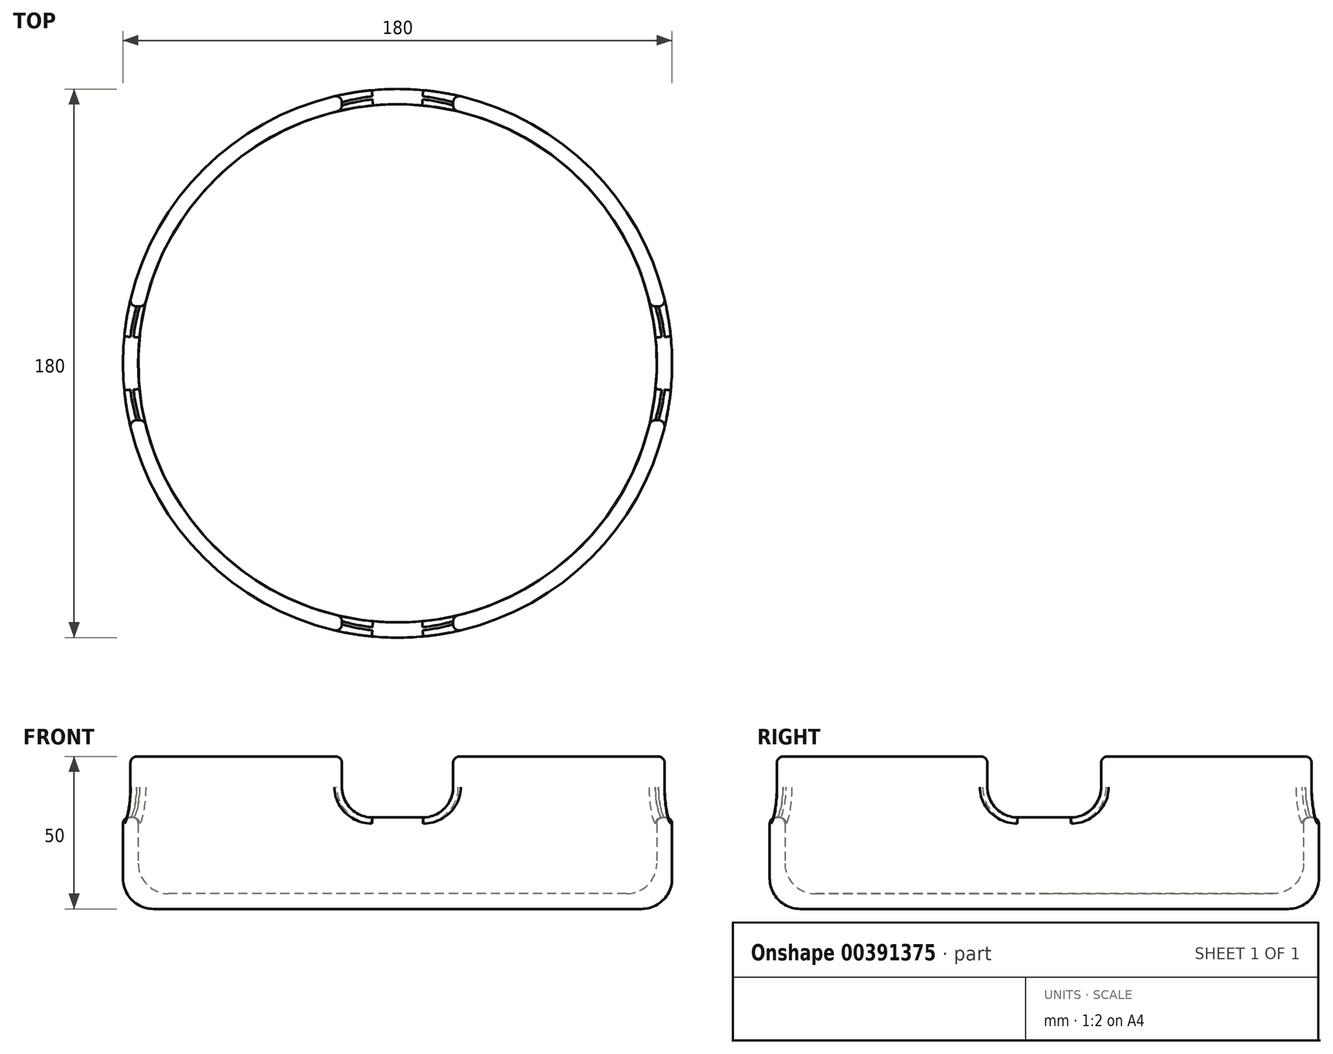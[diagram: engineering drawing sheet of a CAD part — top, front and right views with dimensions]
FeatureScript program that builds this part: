
annotation { "Feature Type Name" : "Feature", "Feature Type Description" : "" }
export const myFeature = defineFeature(function(context is Context, id is Id, definition is map)
    precondition{}
    {
        {
            var Q0;
            Q0=qCreatedBy(makeId("Top.planeOp"),FACE);
            var sketch = newSketch(context, id + "F0", { "sketchPlane" : qUnion([Q0])});
            skCircle(sketch, "E0", {"center": v(0, 0) * mm, "radius": 90 * mm});
            skSolve(sketch);
        }
        {
            var Q0;
            Q0=makeQuery(id+"F0.imprint","IMPRINT",FACE,{"disambiguationData":[TD([[makeQuery(id+"F0.imprint","IMPRINT",EDGE,{"derivedFrom":sQuery(id+"F0.wireOp",EDGE,"E0")}),1.0]])]});
            extrude(context, id + "F1", {"entities" : qUnion([Q0]), "depth" : 50 * mm});
        }
        {
            var Q0;
            Q0=makeQuery(id+"F1.opExtrude","CAP_FACE",FACE,{"disambiguationData":[OSD([sQuery(id+"F0.wireOp",EDGE,"E0")])],"isStart":false});
            shell(context, id + "F2", {"entities" : qUnion([Q0]), "thickness" : 5 * mm});
        }
        {
            var Q0;
            Q0=qCreatedBy(makeId("Top.planeOp"),FACE);
            cPlane(context, id + "F3", {"entities" : qUnion([Q0]), "cplaneType" : CPlaneType.OFFSET, "offset" : 50 * mm, "width" : 152.4 * mm, "height" : 152.4 * mm});
        }
        {
            var Q0;
            Q0=qCreatedBy(id+"F3.planeOp",FACE);
            var sketch = newSketch(context, id + "F4", { "sketchPlane" : qUnion([Q0])});
            skLineSegment(sketch, "E1.bottom", {"start": v(18.24, -119.27) * mm, "end": v(-18.24, -119.27) * mm});
            skLineSegment(sketch, "E1.top", {"start": v(18.24, 119.27) * mm, "end": v(-18.24, 119.27) * mm});
            skLineSegment(sketch, "E1.left", {"start": v(18.24, -119.27) * mm, "end": v(18.24, 119.27) * mm});
            skLineSegment(sketch, "E1.right", {"start": v(-18.24, -119.27) * mm, "end": v(-18.24, 119.27) * mm});
            skPoint(sketch, "E1.middle", {"position": v(0, 0) * mm});
            skLineSegment(sketch, "E2.bottom", {"start": v(-104.63, 18.65) * mm, "end": v(104.63, 18.65) * mm});
            skLineSegment(sketch, "E2.top", {"start": v(-104.63, -18.65) * mm, "end": v(104.63, -18.65) * mm});
            skLineSegment(sketch, "E2.left", {"start": v(-104.63, 18.65) * mm, "end": v(-104.63, -18.65) * mm});
            skLineSegment(sketch, "E2.right", {"start": v(104.63, 18.65) * mm, "end": v(104.63, -18.65) * mm});
            skSolve(sketch);
        }
        {
            var Q0;
            {var subQ0=sQuery(id+"F4.wireOp",EDGE,"E1.bottom");Q0=makeQuery(id+"F4.imprint","IMPRINT",FACE,{"disambiguationData":[TD([[makeQuery(id+"F4.imprint","IMPRINT",EDGE,{"derivedFrom":subQ0}),-1.0]])]});}
            var Q1;
            {var subQ5=sQuery(id+"F4.wireOp",EDGE,"E2.right");Q1=makeQuery(id+"F4.imprint","IMPRINT",FACE,{"disambiguationData":[TD([[makeQuery(id+"F4.imprint","IMPRINT",EDGE,{"derivedFrom":subQ5}),-1.0]])]});}
            var Q2;
            {var subQ0=sQuery(id+"F4.wireOp",EDGE,"E1.top");Q2=makeQuery(id+"F4.imprint","IMPRINT",FACE,{"disambiguationData":[TD([[makeQuery(id+"F4.imprint","IMPRINT",EDGE,{"derivedFrom":subQ0}),1.0]])]});}
            var Q3;
            {var subQ5=sQuery(id+"F4.wireOp",EDGE,"E2.left");Q3=makeQuery(id+"F4.imprint","IMPRINT",FACE,{"disambiguationData":[TD([[makeQuery(id+"F4.imprint","IMPRINT",EDGE,{"derivedFrom":subQ5}),1.0]])]});}
            extrude(context, id + "F5", {"entities" : qUnion([Q0, Q1, Q2, Q3]), "oppositeDirection" : true, "depth" : 20 * mm});
        }
        {
            var Q0;
            {var subQ0=sQuery(id+"F4.wireOp",EDGE,"E1.left");Q0=makeQuery(id+"F5.opExtrude","CAP_EDGE",EDGE,{"disambiguationData":[OSD([subQ0]),TDD([makeQuery(id+"F4.imprint","IMPRINT",EDGE,{"disambiguationData":[TD([[makeQuery(id+"F4.imprint","INTERSECT",VERTEX,{"derivedFrom":[sQuery(id+"F4.wireOp",EDGE,"E1.bottom"),subQ0]}),-1.0]])],"derivedFrom":subQ0})])],"isStart":false});}
            var Q1;
            {var subQ0=sQuery(id+"F4.wireOp",EDGE,"E1.right");Q1=makeQuery(id+"F5.opExtrude","CAP_EDGE",EDGE,{"disambiguationData":[OSD([subQ0]),TDD([makeQuery(id+"F4.imprint","IMPRINT",EDGE,{"disambiguationData":[TD([[makeQuery(id+"F4.imprint","INTERSECT",VERTEX,{"derivedFrom":[sQuery(id+"F4.wireOp",EDGE,"E1.bottom"),subQ0]}),-1.0]])],"derivedFrom":subQ0})])],"isStart":false});}
            var Q2;
            {var subQ0=sQuery(id+"F4.wireOp",EDGE,"E2.top");Q2=makeQuery(id+"F5.opExtrude","CAP_EDGE",EDGE,{"disambiguationData":[OSD([subQ0]),TDD([makeQuery(id+"F4.imprint","IMPRINT",EDGE,{"disambiguationData":[TD([[makeQuery(id+"F4.imprint","INTERSECT",VERTEX,{"derivedFrom":[subQ0,sQuery(id+"F4.wireOp",EDGE,"E2.left")]}),-1.0]])],"derivedFrom":subQ0})])],"isStart":false});}
            var Q3;
            {var subQ0=sQuery(id+"F4.wireOp",EDGE,"E2.bottom");Q3=makeQuery(id+"F5.opExtrude","CAP_EDGE",EDGE,{"disambiguationData":[OSD([subQ0]),TDD([makeQuery(id+"F4.imprint","IMPRINT",EDGE,{"disambiguationData":[TD([[makeQuery(id+"F4.imprint","INTERSECT",VERTEX,{"derivedFrom":[subQ0,sQuery(id+"F4.wireOp",EDGE,"E2.left")]}),-1.0]])],"derivedFrom":subQ0})])],"isStart":false});}
            var Q4;
            {var subQ0=sQuery(id+"F4.wireOp",EDGE,"E1.right");Q4=makeQuery(id+"F5.opExtrude","CAP_EDGE",EDGE,{"disambiguationData":[OSD([subQ0]),TDD([makeQuery(id+"F4.imprint","IMPRINT",EDGE,{"disambiguationData":[TD([[makeQuery(id+"F4.imprint","INTERSECT",VERTEX,{"derivedFrom":[sQuery(id+"F4.wireOp",EDGE,"E1.top"),subQ0]}),1.0]])],"derivedFrom":subQ0})])],"isStart":false});}
            var Q5;
            {var subQ0=sQuery(id+"F4.wireOp",EDGE,"E1.left");Q5=makeQuery(id+"F5.opExtrude","CAP_EDGE",EDGE,{"disambiguationData":[OSD([subQ0]),TDD([makeQuery(id+"F4.imprint","IMPRINT",EDGE,{"disambiguationData":[TD([[makeQuery(id+"F4.imprint","INTERSECT",VERTEX,{"derivedFrom":[sQuery(id+"F4.wireOp",EDGE,"E1.top"),subQ0]}),1.0]])],"derivedFrom":subQ0})])],"isStart":false});}
            var Q6;
            {var subQ0=sQuery(id+"F4.wireOp",EDGE,"E2.bottom");Q6=makeQuery(id+"F5.opExtrude","CAP_EDGE",EDGE,{"disambiguationData":[OSD([subQ0]),TDD([makeQuery(id+"F4.imprint","IMPRINT",EDGE,{"disambiguationData":[TD([[makeQuery(id+"F4.imprint","INTERSECT",VERTEX,{"derivedFrom":[subQ0,sQuery(id+"F4.wireOp",EDGE,"E2.right")]}),1.0]])],"derivedFrom":subQ0})])],"isStart":false});}
            var Q7;
            {var subQ0=sQuery(id+"F4.wireOp",EDGE,"E2.top");Q7=makeQuery(id+"F5.opExtrude","CAP_EDGE",EDGE,{"disambiguationData":[OSD([subQ0]),TDD([makeQuery(id+"F4.imprint","IMPRINT",EDGE,{"disambiguationData":[TD([[makeQuery(id+"F4.imprint","INTERSECT",VERTEX,{"derivedFrom":[subQ0,sQuery(id+"F4.wireOp",EDGE,"E2.right")]}),1.0]])],"derivedFrom":subQ0})])],"isStart":false});}
            fillet(context, id + "F6", {"entities" : qUnion([Q0, Q1, Q2, Q3, Q4, Q5, Q6, Q7]), "radius" : 10 * mm, "tangentPropagation" : true, "allowEdgeOverflow" : false});
        }
        {
            var Q0;
            Q0=makeQuery(id+"F5.opExtrude","SWEPT_BODY",BODY,{"disambiguationData":[OSD([sQuery(id+"F4.wireOp",EDGE,"E1.top"),sQuery(id+"F4.wireOp",EDGE,"E1.left"),sQuery(id+"F4.wireOp",EDGE,"E1.right"),sQuery(id+"F4.wireOp",EDGE,"E2.bottom")])]});
            var Q1;
            Q1=makeQuery(id+"F5.opExtrude","SWEPT_BODY",BODY,{"disambiguationData":[OSD([sQuery(id+"F4.wireOp",EDGE,"E1.right"),sQuery(id+"F4.wireOp",EDGE,"E2.bottom"),sQuery(id+"F4.wireOp",EDGE,"E2.top"),sQuery(id+"F4.wireOp",EDGE,"E2.left")])]});
            var Q2;
            Q2=makeQuery(id+"F5.opExtrude","SWEPT_BODY",BODY,{"disambiguationData":[OSD([sQuery(id+"F4.wireOp",EDGE,"E1.left"),sQuery(id+"F4.wireOp",EDGE,"E2.bottom"),sQuery(id+"F4.wireOp",EDGE,"E2.top"),sQuery(id+"F4.wireOp",EDGE,"E2.right")])]});
            var Q3;
            Q3=makeQuery(id+"F5.opExtrude","SWEPT_BODY",BODY,{"disambiguationData":[OSD([sQuery(id+"F4.wireOp",EDGE,"E1.bottom"),sQuery(id+"F4.wireOp",EDGE,"E1.left"),sQuery(id+"F4.wireOp",EDGE,"E1.right"),sQuery(id+"F4.wireOp",EDGE,"E2.top")])]});
            var Q4;
            Q4=makeQuery(id+"F1.opExtrude","SWEPT_BODY",BODY,{"disambiguationData":[OSD([sQuery(id+"F0.wireOp",EDGE,"E0")])]});
            booleanBodies(context, id + "F7", {"operationType" : BooleanOperationType.SUBTRACTION, "tools" : qUnion([Q0, Q1, Q2, Q3]), "targets" : qUnion([Q4])});
        }
        {
            var Q0;
            Q0=makeQuery(id+"F1.opExtrude","CAP_EDGE",EDGE,{"disambiguationData":[OSD([sQuery(id+"F0.wireOp",EDGE,"E0")])],"isStart":true});
            fillet(context, id + "F8", {"entities" : qUnion([Q0]), "radius" : 10 * mm, "tangentPropagation" : true, "allowEdgeOverflow" : false});
        }
        {
            var Q0;
            {var subQ0=sQuery(id+"F0.wireOp",EDGE,"E0");var subQ3=sQuery(id+"F4.wireOp",EDGE,"E1.left");Q0=makeQuery(id+"F7.opBoolean","SPLIT",FACE,{"disambiguationData":[TD([makeQuery(id+"F5.opExtrude","SWEPT_FACE",FACE,{"disambiguationData":[OSD([subQ3]),TDD([makeQuery(id+"F4.imprint","IMPRINT",EDGE,{"disambiguationData":[TD([[makeQuery(id+"F4.imprint","INTERSECT",VERTEX,{"derivedFrom":[sQuery(id+"F4.wireOp",EDGE,"E1.top"),subQ3]}),1.0]])],"derivedFrom":subQ3})])]})])],"derivedFrom":makeQuery(id+"F1.opExtrude","CAP_FACE",FACE,{"disambiguationData":[OSD([subQ0])],"isStart":false})});}
            var Q1;
            {var subQ0=sQuery(id+"F4.wireOp",EDGE,"E2.bottom");Q1=makeQuery(id+"F7.opBoolean","COPY",FACE,{"derivedFrom":makeQuery(id+"F5.opExtrude","SWEPT_FACE",FACE,{"disambiguationData":[OSD([subQ0]),TDD([makeQuery(id+"F4.imprint","IMPRINT",EDGE,{"disambiguationData":[TD([[makeQuery(id+"F4.imprint","INTERSECT",VERTEX,{"derivedFrom":[subQ0,sQuery(id+"F4.wireOp",EDGE,"E2.right")]}),1.0]])],"derivedFrom":subQ0})])]})});}
            var Q2;
            {var subQ0=sQuery(id+"F4.wireOp",EDGE,"E2.bottom");Q2=makeQuery(id+"F7.opBoolean","COPY",FACE,{"derivedFrom":makeQuery(id+"F6.opFillet","BLEND_FACE",FACE,{"disambiguationData":[OSD([subQ0]),TDD([makeQuery(id+"F5.opExtrude","CAP_EDGE",EDGE,{"disambiguationData":[OSD([subQ0]),TDD([makeQuery(id+"F4.imprint","IMPRINT",EDGE,{"disambiguationData":[TD([[makeQuery(id+"F4.imprint","INTERSECT",VERTEX,{"derivedFrom":[subQ0,sQuery(id+"F4.wireOp",EDGE,"E2.right")]}),1.0]])],"derivedFrom":subQ0})])],"isStart":false})])]})});}
            var Q3;
            Q3=makeQuery(id+"F7.opBoolean","COPY",FACE,{"derivedFrom":makeQuery(id+"F5.opExtrude","CAP_FACE",FACE,{"disambiguationData":[OSD([sQuery(id+"F4.wireOp",EDGE,"E1.left"),sQuery(id+"F4.wireOp",EDGE,"E2.bottom"),sQuery(id+"F4.wireOp",EDGE,"E2.top"),sQuery(id+"F4.wireOp",EDGE,"E2.right")])],"isStart":false})});
            var Q4;
            {var subQ0=sQuery(id+"F4.wireOp",EDGE,"E2.top");Q4=makeQuery(id+"F7.opBoolean","COPY",FACE,{"derivedFrom":makeQuery(id+"F6.opFillet","BLEND_FACE",FACE,{"disambiguationData":[OSD([subQ0]),TDD([makeQuery(id+"F5.opExtrude","CAP_EDGE",EDGE,{"disambiguationData":[OSD([subQ0]),TDD([makeQuery(id+"F4.imprint","IMPRINT",EDGE,{"disambiguationData":[TD([[makeQuery(id+"F4.imprint","INTERSECT",VERTEX,{"derivedFrom":[subQ0,sQuery(id+"F4.wireOp",EDGE,"E2.right")]}),1.0]])],"derivedFrom":subQ0})])],"isStart":false})])]})});}
            var Q5;
            {var subQ0=sQuery(id+"F4.wireOp",EDGE,"E2.top");Q5=makeQuery(id+"F7.opBoolean","COPY",FACE,{"derivedFrom":makeQuery(id+"F5.opExtrude","SWEPT_FACE",FACE,{"disambiguationData":[OSD([subQ0]),TDD([makeQuery(id+"F4.imprint","IMPRINT",EDGE,{"disambiguationData":[TD([[makeQuery(id+"F4.imprint","INTERSECT",VERTEX,{"derivedFrom":[subQ0,sQuery(id+"F4.wireOp",EDGE,"E2.right")]}),1.0]])],"derivedFrom":subQ0})])]})});}
            var Q6;
            {var subQ0=sQuery(id+"F0.wireOp",EDGE,"E0");var subQ2=sQuery(id+"F4.wireOp",EDGE,"E1.left");Q6=makeQuery(id+"F7.opBoolean","SPLIT",FACE,{"disambiguationData":[TD([makeQuery(id+"F5.opExtrude","SWEPT_FACE",FACE,{"disambiguationData":[OSD([subQ2]),TDD([makeQuery(id+"F4.imprint","IMPRINT",EDGE,{"disambiguationData":[TD([[makeQuery(id+"F4.imprint","INTERSECT",VERTEX,{"derivedFrom":[sQuery(id+"F4.wireOp",EDGE,"E1.bottom"),subQ2]}),-1.0]])],"derivedFrom":subQ2})])]})])],"derivedFrom":makeQuery(id+"F1.opExtrude","CAP_FACE",FACE,{"disambiguationData":[OSD([subQ0])],"isStart":false})});}
            var Q7;
            {var subQ0=sQuery(id+"F4.wireOp",EDGE,"E1.left");Q7=makeQuery(id+"F7.opBoolean","COPY",FACE,{"derivedFrom":makeQuery(id+"F6.opFillet","BLEND_FACE",FACE,{"disambiguationData":[OSD([subQ0]),TDD([makeQuery(id+"F5.opExtrude","CAP_EDGE",EDGE,{"disambiguationData":[OSD([subQ0]),TDD([makeQuery(id+"F4.imprint","IMPRINT",EDGE,{"disambiguationData":[TD([[makeQuery(id+"F4.imprint","INTERSECT",VERTEX,{"derivedFrom":[sQuery(id+"F4.wireOp",EDGE,"E1.bottom"),subQ0]}),-1.0]])],"derivedFrom":subQ0})])],"isStart":false})])]})});}
            var Q8;
            Q8=makeQuery(id+"F7.opBoolean","COPY",FACE,{"derivedFrom":makeQuery(id+"F5.opExtrude","CAP_FACE",FACE,{"disambiguationData":[OSD([sQuery(id+"F4.wireOp",EDGE,"E1.bottom"),sQuery(id+"F4.wireOp",EDGE,"E1.left"),sQuery(id+"F4.wireOp",EDGE,"E1.right"),sQuery(id+"F4.wireOp",EDGE,"E2.top")])],"isStart":false})});
            var Q9;
            {var subQ0=sQuery(id+"F4.wireOp",EDGE,"E1.right");Q9=makeQuery(id+"F7.opBoolean","COPY",FACE,{"derivedFrom":makeQuery(id+"F6.opFillet","BLEND_FACE",FACE,{"disambiguationData":[OSD([subQ0]),TDD([makeQuery(id+"F5.opExtrude","CAP_EDGE",EDGE,{"disambiguationData":[OSD([subQ0]),TDD([makeQuery(id+"F4.imprint","IMPRINT",EDGE,{"disambiguationData":[TD([[makeQuery(id+"F4.imprint","INTERSECT",VERTEX,{"derivedFrom":[sQuery(id+"F4.wireOp",EDGE,"E1.bottom"),subQ0]}),-1.0]])],"derivedFrom":subQ0})])],"isStart":false})])]})});}
            var Q10;
            {var subQ0=sQuery(id+"F4.wireOp",EDGE,"E1.right");Q10=makeQuery(id+"F7.opBoolean","COPY",FACE,{"derivedFrom":makeQuery(id+"F5.opExtrude","SWEPT_FACE",FACE,{"disambiguationData":[OSD([subQ0]),TDD([makeQuery(id+"F4.imprint","IMPRINT",EDGE,{"disambiguationData":[TD([[makeQuery(id+"F4.imprint","INTERSECT",VERTEX,{"derivedFrom":[sQuery(id+"F4.wireOp",EDGE,"E1.bottom"),subQ0]}),-1.0]])],"derivedFrom":subQ0})])]})});}
            var Q11;
            {var subQ0=sQuery(id+"F0.wireOp",EDGE,"E0");var subQ3=sQuery(id+"F4.wireOp",EDGE,"E1.right");Q11=makeQuery(id+"F7.opBoolean","SPLIT",FACE,{"disambiguationData":[TD([makeQuery(id+"F5.opExtrude","SWEPT_FACE",FACE,{"disambiguationData":[OSD([subQ3]),TDD([makeQuery(id+"F4.imprint","IMPRINT",EDGE,{"disambiguationData":[TD([[makeQuery(id+"F4.imprint","INTERSECT",VERTEX,{"derivedFrom":[sQuery(id+"F4.wireOp",EDGE,"E1.bottom"),subQ3]}),-1.0]])],"derivedFrom":subQ3})])]})])],"derivedFrom":makeQuery(id+"F1.opExtrude","CAP_FACE",FACE,{"disambiguationData":[OSD([subQ0])],"isStart":false})});}
            var Q12;
            {var subQ0=sQuery(id+"F4.wireOp",EDGE,"E1.left");Q12=makeQuery(id+"F7.opBoolean","COPY",FACE,{"derivedFrom":makeQuery(id+"F5.opExtrude","SWEPT_FACE",FACE,{"disambiguationData":[OSD([subQ0]),TDD([makeQuery(id+"F4.imprint","IMPRINT",EDGE,{"disambiguationData":[TD([[makeQuery(id+"F4.imprint","INTERSECT",VERTEX,{"derivedFrom":[sQuery(id+"F4.wireOp",EDGE,"E1.bottom"),subQ0]}),-1.0]])],"derivedFrom":subQ0})])]})});}
            var Q13;
            {var subQ0=sQuery(id+"F4.wireOp",EDGE,"E2.top");Q13=makeQuery(id+"F7.opBoolean","COPY",FACE,{"derivedFrom":makeQuery(id+"F5.opExtrude","SWEPT_FACE",FACE,{"disambiguationData":[OSD([subQ0]),TDD([makeQuery(id+"F4.imprint","IMPRINT",EDGE,{"disambiguationData":[TD([[makeQuery(id+"F4.imprint","INTERSECT",VERTEX,{"derivedFrom":[subQ0,sQuery(id+"F4.wireOp",EDGE,"E2.left")]}),-1.0]])],"derivedFrom":subQ0})])]})});}
            var Q14;
            {var subQ0=sQuery(id+"F4.wireOp",EDGE,"E2.top");Q14=makeQuery(id+"F7.opBoolean","COPY",FACE,{"derivedFrom":makeQuery(id+"F6.opFillet","BLEND_FACE",FACE,{"disambiguationData":[OSD([subQ0]),TDD([makeQuery(id+"F5.opExtrude","CAP_EDGE",EDGE,{"disambiguationData":[OSD([subQ0]),TDD([makeQuery(id+"F4.imprint","IMPRINT",EDGE,{"disambiguationData":[TD([[makeQuery(id+"F4.imprint","INTERSECT",VERTEX,{"derivedFrom":[subQ0,sQuery(id+"F4.wireOp",EDGE,"E2.left")]}),-1.0]])],"derivedFrom":subQ0})])],"isStart":false})])]})});}
            var Q15;
            Q15=makeQuery(id+"F7.opBoolean","COPY",FACE,{"derivedFrom":makeQuery(id+"F5.opExtrude","CAP_FACE",FACE,{"disambiguationData":[OSD([sQuery(id+"F4.wireOp",EDGE,"E1.right"),sQuery(id+"F4.wireOp",EDGE,"E2.bottom"),sQuery(id+"F4.wireOp",EDGE,"E2.top"),sQuery(id+"F4.wireOp",EDGE,"E2.left")])],"isStart":false})});
            var Q16;
            {var subQ0=sQuery(id+"F4.wireOp",EDGE,"E2.bottom");Q16=makeQuery(id+"F7.opBoolean","COPY",FACE,{"derivedFrom":makeQuery(id+"F6.opFillet","BLEND_FACE",FACE,{"disambiguationData":[OSD([subQ0]),TDD([makeQuery(id+"F5.opExtrude","CAP_EDGE",EDGE,{"disambiguationData":[OSD([subQ0]),TDD([makeQuery(id+"F4.imprint","IMPRINT",EDGE,{"disambiguationData":[TD([[makeQuery(id+"F4.imprint","INTERSECT",VERTEX,{"derivedFrom":[subQ0,sQuery(id+"F4.wireOp",EDGE,"E2.left")]}),-1.0]])],"derivedFrom":subQ0})])],"isStart":false})])]})});}
            var Q17;
            {var subQ0=sQuery(id+"F4.wireOp",EDGE,"E2.bottom");Q17=makeQuery(id+"F7.opBoolean","COPY",FACE,{"derivedFrom":makeQuery(id+"F5.opExtrude","SWEPT_FACE",FACE,{"disambiguationData":[OSD([subQ0]),TDD([makeQuery(id+"F4.imprint","IMPRINT",EDGE,{"disambiguationData":[TD([[makeQuery(id+"F4.imprint","INTERSECT",VERTEX,{"derivedFrom":[subQ0,sQuery(id+"F4.wireOp",EDGE,"E2.left")]}),-1.0]])],"derivedFrom":subQ0})])]})});}
            var Q18;
            {var subQ0=sQuery(id+"F0.wireOp",EDGE,"E0");var subQ2=sQuery(id+"F4.wireOp",EDGE,"E1.right");Q18=makeQuery(id+"F7.opBoolean","SPLIT",FACE,{"disambiguationData":[TD([makeQuery(id+"F5.opExtrude","SWEPT_FACE",FACE,{"disambiguationData":[OSD([subQ2]),TDD([makeQuery(id+"F4.imprint","IMPRINT",EDGE,{"disambiguationData":[TD([[makeQuery(id+"F4.imprint","INTERSECT",VERTEX,{"derivedFrom":[sQuery(id+"F4.wireOp",EDGE,"E1.top"),subQ2]}),1.0]])],"derivedFrom":subQ2})])]})])],"derivedFrom":makeQuery(id+"F1.opExtrude","CAP_FACE",FACE,{"disambiguationData":[OSD([subQ0])],"isStart":false})});}
            var Q19;
            {var subQ0=sQuery(id+"F4.wireOp",EDGE,"E1.right");Q19=makeQuery(id+"F7.opBoolean","COPY",FACE,{"derivedFrom":makeQuery(id+"F6.opFillet","BLEND_FACE",FACE,{"disambiguationData":[OSD([subQ0]),TDD([makeQuery(id+"F5.opExtrude","CAP_EDGE",EDGE,{"disambiguationData":[OSD([subQ0]),TDD([makeQuery(id+"F4.imprint","IMPRINT",EDGE,{"disambiguationData":[TD([[makeQuery(id+"F4.imprint","INTERSECT",VERTEX,{"derivedFrom":[sQuery(id+"F4.wireOp",EDGE,"E1.top"),subQ0]}),1.0]])],"derivedFrom":subQ0})])],"isStart":false})])]})});}
            var Q20;
            Q20=makeQuery(id+"F7.opBoolean","COPY",FACE,{"derivedFrom":makeQuery(id+"F5.opExtrude","CAP_FACE",FACE,{"disambiguationData":[OSD([sQuery(id+"F4.wireOp",EDGE,"E1.top"),sQuery(id+"F4.wireOp",EDGE,"E1.left"),sQuery(id+"F4.wireOp",EDGE,"E1.right"),sQuery(id+"F4.wireOp",EDGE,"E2.bottom")])],"isStart":false})});
            var Q21;
            {var subQ0=sQuery(id+"F4.wireOp",EDGE,"E1.right");Q21=makeQuery(id+"F7.opBoolean","COPY",FACE,{"derivedFrom":makeQuery(id+"F5.opExtrude","SWEPT_FACE",FACE,{"disambiguationData":[OSD([subQ0]),TDD([makeQuery(id+"F4.imprint","IMPRINT",EDGE,{"disambiguationData":[TD([[makeQuery(id+"F4.imprint","INTERSECT",VERTEX,{"derivedFrom":[sQuery(id+"F4.wireOp",EDGE,"E1.top"),subQ0]}),1.0]])],"derivedFrom":subQ0})])]})});}
            var Q22;
            {var subQ0=sQuery(id+"F4.wireOp",EDGE,"E1.left");Q22=makeQuery(id+"F7.opBoolean","COPY",FACE,{"derivedFrom":makeQuery(id+"F6.opFillet","BLEND_FACE",FACE,{"disambiguationData":[OSD([subQ0]),TDD([makeQuery(id+"F5.opExtrude","CAP_EDGE",EDGE,{"disambiguationData":[OSD([subQ0]),TDD([makeQuery(id+"F4.imprint","IMPRINT",EDGE,{"disambiguationData":[TD([[makeQuery(id+"F4.imprint","INTERSECT",VERTEX,{"derivedFrom":[sQuery(id+"F4.wireOp",EDGE,"E1.top"),subQ0]}),1.0]])],"derivedFrom":subQ0})])],"isStart":false})])]})});}
            var Q23;
            {var subQ0=sQuery(id+"F4.wireOp",EDGE,"E1.left");Q23=makeQuery(id+"F7.opBoolean","COPY",FACE,{"derivedFrom":makeQuery(id+"F5.opExtrude","SWEPT_FACE",FACE,{"disambiguationData":[OSD([subQ0]),TDD([makeQuery(id+"F4.imprint","IMPRINT",EDGE,{"disambiguationData":[TD([[makeQuery(id+"F4.imprint","INTERSECT",VERTEX,{"derivedFrom":[sQuery(id+"F4.wireOp",EDGE,"E1.top"),subQ0]}),1.0]])],"derivedFrom":subQ0})])]})});}
            var Q24;
            Q24=makeQuery(id+"F1.opExtrude","SWEPT_FACE",FACE,{"disambiguationData":[OSD([sQuery(id+"F0.wireOp",EDGE,"E0")])]});
            fillet(context, id + "F9", {"entities" : qUnion([Q0, Q1, Q2, Q3, Q4, Q5, Q6, Q7, Q8, Q9, Q10, Q11, Q12, Q13, Q14, Q15, Q16, Q17, Q18, Q19, Q20, Q21, Q22, Q23, Q24]), "radius" : 2 * mm, "tangentPropagation" : true, "allowEdgeOverflow" : false});
        }
        {
            var Q0;
            {var subQ0=sQuery(id+"F0.wireOp",EDGE,"E0");Q0=makeQuery(id+"F2.opShell","OFFSET_EDGE",EDGE,{"disambiguationData":[OSD([subQ0]),TDD([makeQuery(id+"F1.opExtrude","CAP_EDGE",EDGE,{"disambiguationData":[OSD([subQ0])],"isStart":true})])]});}
            fillet(context, id + "F10", {"entities" : qUnion([Q0]), "radius" : 10 * mm, "tangentPropagation" : true, "allowEdgeOverflow" : false});
        }
    });
